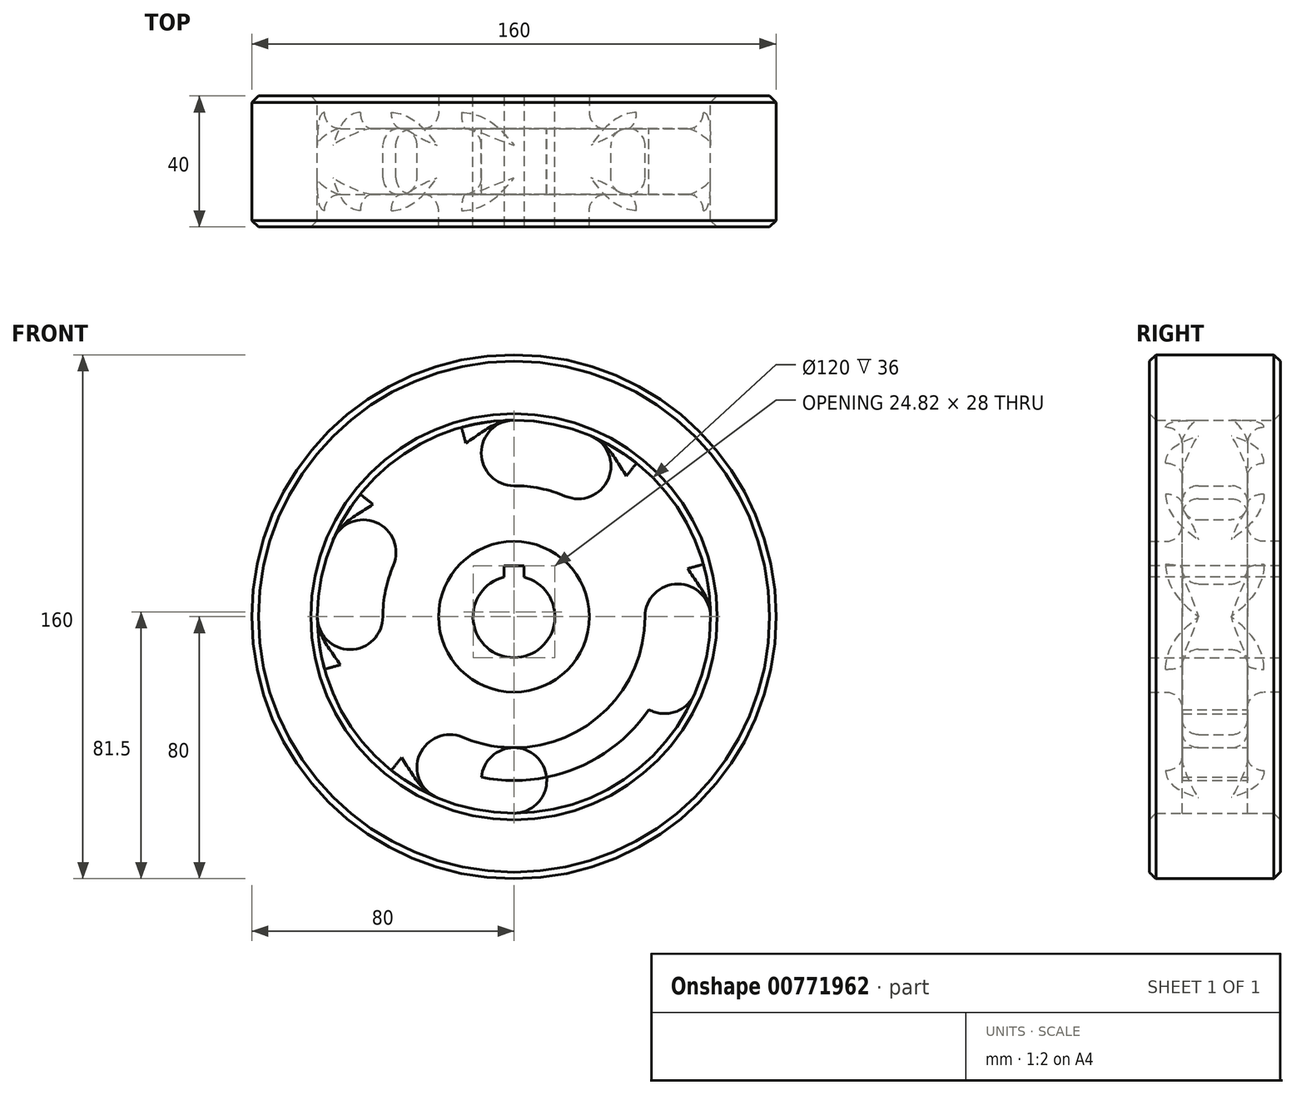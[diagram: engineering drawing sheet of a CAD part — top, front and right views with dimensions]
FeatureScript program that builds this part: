
annotation { "Feature Type Name" : "Feature", "Feature Type Description" : "" }
export const myFeature = defineFeature(function(context is Context, id is Id, definition is map)
    precondition{}
    {
        {
            var Q0;
            Q0=qCreatedBy(makeId("Front.planeOp"),FACE);
            var sketch = newSketch(context, id + "F0", { "sketchPlane" : qUnion([Q0])});
            skCircle(sketch, "E0", {"center": v(0, 0) * mm, "radius": 80 * mm});
            skCircle(sketch, "E1", {"center": v(0, 0) * mm, "radius": 60 * mm});
            skPoint(sketch, "E2", {"position": v(0, 60) * mm});
            skPoint(sketch, "E3", {"position": v(-60, 0) * mm});
            skPoint(sketch, "E4", {"position": v(60, 0) * mm});
            skPoint(sketch, "E5", {"position": v(0, -60) * mm});
            skCircle(sketch, "E6", {"center": v(0, 0) * mm, "radius": 50 * mm});
            skPoint(sketch, "E7", {"position": v(0, 50) * mm});
            skPoint(sketch, "E8", {"position": v(-50, 0) * mm});
            skPoint(sketch, "E9", {"position": v(0, -50) * mm});
            skPoint(sketch, "E10", {"position": v(50, 0) * mm});
            skCircle(sketch, "E11", {"center": v(0, 50) * mm, "radius": 10 * mm});
            skCircle(sketch, "E12", {"center": v(-50, 0) * mm, "radius": 10 * mm});
            skCircle(sketch, "E13", {"center": v(0, -50) * mm, "radius": 10 * mm});
            skCircle(sketch, "E14", {"center": v(50, 0) * mm, "radius": 10 * mm});
            skPoint(sketch, "E15", {"position": v(-46, 19.6) * mm});
            skPoint(sketch, "E16", {"position": v(19.6, 46) * mm});
            skPoint(sketch, "E17", {"position": v(46, -19.6) * mm});
            skPoint(sketch, "E18", {"position": v(-19.6, -46) * mm});
            skCircle(sketch, "E19", {"center": v(-46, 19.6) * mm, "radius": 10 * mm});
            skCircle(sketch, "E20", {"center": v(19.6, 46) * mm, "radius": 10 * mm});
            skCircle(sketch, "E21", {"center": v(46, -19.6) * mm, "radius": 10 * mm});
            skCircle(sketch, "E22", {"center": v(-19.6, -46) * mm, "radius": 10 * mm});
            skCircle(sketch, "E23", {"center": v(0, 0) * mm, "radius": 40 * mm});
            skCircle(sketch, "E24", {"center": v(0, 0) * mm, "radius": 23 * mm});
            skCircle(sketch, "E25", {"center": v(0, 0) * mm, "radius": 12.5 * mm});
            skSolve(sketch);
        }
        {
            var Q0;
            Q0=makeQuery(id+"F0.imprint","IMPRINT",FACE,{"disambiguationData":[TD([[makeQuery(id+"F0.imprint","IMPRINT",EDGE,{"derivedFrom":sQuery(id+"F0.wireOp",EDGE,"E0")}),1.0]])]});
            extrude(context, id + "F1", {"entities" : qUnion([Q0]), "depth" : 20 * mm, "offsetDistance" : 25 * mm});
        }
        {
            var Q0;
            {var subQ0=sQuery(id+"F0.wireOp",EDGE,"E11");var subQ1=sQuery(id+"F0.wireOp",EDGE,"E6");var subQ2=makeQuery(id+"F0.imprint","INTERSECT",VERTEX,{"disambiguationData":[OD(1.0)],"derivedFrom":[subQ1,subQ0]});Q0=makeQuery(id+"F0.imprint","IMPRINT",FACE,{"disambiguationData":[TD([[makeQuery(id+"F0.imprint","IMPRINT",EDGE,{"disambiguationData":[TD([[subQ2,-1.0]])],"derivedFrom":subQ1}),1.0]])]});}
            var Q1;
            {var subQ0=sQuery(id+"F0.wireOp",EDGE,"E11");var subQ1=sQuery(id+"F0.wireOp",EDGE,"E1");var subQ2=makeQuery(id+"F0.imprint","INTERSECT",VERTEX,{"derivedFrom":[subQ1,subQ0]});Q1=makeQuery(id+"F0.imprint","IMPRINT",FACE,{"disambiguationData":[TD([[makeQuery(id+"F0.imprint","IMPRINT",EDGE,{"disambiguationData":[TD([[subQ2,-1.0]])],"derivedFrom":subQ1}),1.0]])]});}
            var Q2;
            {var subQ0=sQuery(id+"F0.wireOp",EDGE,"E12");var subQ1=sQuery(id+"F0.wireOp",EDGE,"E1");var subQ2=makeQuery(id+"F0.imprint","INTERSECT",VERTEX,{"derivedFrom":[subQ1,subQ0]});Q2=makeQuery(id+"F0.imprint","IMPRINT",FACE,{"disambiguationData":[TD([[makeQuery(id+"F0.imprint","IMPRINT",EDGE,{"disambiguationData":[TD([[subQ2,-1.0]])],"derivedFrom":subQ1}),1.0]])]});}
            var Q3;
            {var subQ0=sQuery(id+"F0.wireOp",EDGE,"E12");var subQ1=sQuery(id+"F0.wireOp",EDGE,"E6");var subQ2=makeQuery(id+"F0.imprint","INTERSECT",VERTEX,{"disambiguationData":[OD(1.0)],"derivedFrom":[subQ1,subQ0]});Q3=makeQuery(id+"F0.imprint","IMPRINT",FACE,{"disambiguationData":[TD([[makeQuery(id+"F0.imprint","IMPRINT",EDGE,{"disambiguationData":[TD([[subQ2,-1.0]])],"derivedFrom":subQ1}),1.0]])]});}
            var Q4;
            {var subQ0=sQuery(id+"F0.wireOp",EDGE,"E13");var subQ1=sQuery(id+"F0.wireOp",EDGE,"E6");var subQ2=makeQuery(id+"F0.imprint","INTERSECT",VERTEX,{"disambiguationData":[OD(1.0)],"derivedFrom":[subQ1,subQ0]});Q4=makeQuery(id+"F0.imprint","IMPRINT",FACE,{"disambiguationData":[TD([[makeQuery(id+"F0.imprint","IMPRINT",EDGE,{"disambiguationData":[TD([[subQ2,-1.0]])],"derivedFrom":subQ1}),1.0]])]});}
            var Q5;
            {var subQ0=sQuery(id+"F0.wireOp",EDGE,"E13");var subQ1=sQuery(id+"F0.wireOp",EDGE,"E1");var subQ2=makeQuery(id+"F0.imprint","INTERSECT",VERTEX,{"derivedFrom":[subQ1,subQ0]});Q5=makeQuery(id+"F0.imprint","IMPRINT",FACE,{"disambiguationData":[TD([[makeQuery(id+"F0.imprint","IMPRINT",EDGE,{"disambiguationData":[TD([[subQ2,-1.0]])],"derivedFrom":subQ1}),1.0]])]});}
            var Q6;
            {var subQ0=sQuery(id+"F0.wireOp",EDGE,"E20");var subQ1=sQuery(id+"F0.wireOp",EDGE,"E6");var subQ2=makeQuery(id+"F0.imprint","INTERSECT",VERTEX,{"disambiguationData":[OD(0.0)],"derivedFrom":[subQ1,subQ0]});Q6=makeQuery(id+"F0.imprint","IMPRINT",FACE,{"disambiguationData":[TD([[makeQuery(id+"F0.imprint","IMPRINT",EDGE,{"disambiguationData":[TD([[subQ2,1.0]])],"derivedFrom":subQ1}),1.0]])]});}
            var Q7;
            {var subQ0=sQuery(id+"F0.wireOp",EDGE,"E20");var subQ1=sQuery(id+"F0.wireOp",EDGE,"E1");var subQ2=makeQuery(id+"F0.imprint","INTERSECT",VERTEX,{"derivedFrom":[subQ1,subQ0]});Q7=makeQuery(id+"F0.imprint","IMPRINT",FACE,{"disambiguationData":[TD([[makeQuery(id+"F0.imprint","IMPRINT",EDGE,{"disambiguationData":[TD([[subQ2,1.0]])],"derivedFrom":subQ1}),1.0]])]});}
            var Q8;
            Q8=makeQuery(id+"F0.imprint","IMPRINT",FACE,{"disambiguationData":[TD([[makeQuery(id+"F0.imprint","IMPRINT",EDGE,{"derivedFrom":sQuery(id+"F0.wireOp",EDGE,"E24")}),-1.0]])]});
            extrude(context, id + "F2", {"entities" : qUnion([Q0, Q1, Q2, Q3, Q4, Q5, Q6, Q7, Q8]), "operationType" : NewBodyOperationType.ADD, "depth" : 10 * mm, "offsetDistance" : 25 * mm});
        }
        {
            var Q0;
            Q0=makeQuery(id+"F0.imprint","IMPRINT",FACE,{"disambiguationData":[TD([[makeQuery(id+"F0.imprint","IMPRINT",EDGE,{"derivedFrom":sQuery(id+"F0.wireOp",EDGE,"E24")}),1.0]])]});
            extrude(context, id + "F3", {"entities" : qUnion([Q0]), "operationType" : NewBodyOperationType.ADD, "depth" : 20 * mm, "offsetDistance" : 25 * mm});
        }
        {
            var Q0;
            Q0=makeQuery(id+"F0.imprint","IMPRINT",FACE,{"disambiguationData":[TD([[makeQuery(id+"F0.imprint","IMPRINT",EDGE,{"derivedFrom":sQuery(id+"F0.wireOp",EDGE,"E0")}),1.0]])]});
            var Q1;
            Q1=makeQuery(id+"F0.imprint","IMPRINT",FACE,{"disambiguationData":[TD([[makeQuery(id+"F0.imprint","IMPRINT",EDGE,{"derivedFrom":sQuery(id+"F0.wireOp",EDGE,"E24")}),1.0]])]});
            extrude(context, id + "F4", {"entities" : qUnion([Q0, Q1]), "operationType" : NewBodyOperationType.ADD, "depth" : 20 * mm, "offsetDistance" : 25 * mm});
        }
        {
            var Q0;
            Q0=makeQuery(id+"F0.imprint","IMPRINT",FACE,{"disambiguationData":[TD([[makeQuery(id+"F0.imprint","IMPRINT",EDGE,{"derivedFrom":sQuery(id+"F0.wireOp",EDGE,"E0")}),1.0]])]});
            var Q1;
            Q1=makeQuery(id+"F0.imprint","IMPRINT",FACE,{"disambiguationData":[TD([[makeQuery(id+"F0.imprint","IMPRINT",EDGE,{"derivedFrom":sQuery(id+"F0.wireOp",EDGE,"E24")}),1.0]])]});
            extrude(context, id + "F5", {"entities" : qUnion([Q0, Q1]), "operationType" : NewBodyOperationType.ADD, "oppositeDirection" : true, "depth" : 20 * mm, "offsetDistance" : 25 * mm});
        }
        {
            var Q0;
            {var subQ0=sQuery(id+"F0.wireOp",EDGE,"E20");var subQ1=sQuery(id+"F0.wireOp",EDGE,"E6");var subQ2=makeQuery(id+"F0.imprint","INTERSECT",VERTEX,{"disambiguationData":[OD(0.0)],"derivedFrom":[subQ1,subQ0]});Q0=makeQuery(id+"F0.imprint","IMPRINT",FACE,{"disambiguationData":[TD([[makeQuery(id+"F0.imprint","IMPRINT",EDGE,{"disambiguationData":[TD([[subQ2,1.0]])],"derivedFrom":subQ1}),1.0]])]});}
            var Q1;
            {var subQ0=sQuery(id+"F0.wireOp",EDGE,"E20");var subQ1=sQuery(id+"F0.wireOp",EDGE,"E1");var subQ2=makeQuery(id+"F0.imprint","INTERSECT",VERTEX,{"derivedFrom":[subQ1,subQ0]});Q1=makeQuery(id+"F0.imprint","IMPRINT",FACE,{"disambiguationData":[TD([[makeQuery(id+"F0.imprint","IMPRINT",EDGE,{"disambiguationData":[TD([[subQ2,1.0]])],"derivedFrom":subQ1}),1.0]])]});}
            var Q2;
            {var subQ0=sQuery(id+"F0.wireOp",EDGE,"E13");var subQ1=sQuery(id+"F0.wireOp",EDGE,"E6");var subQ2=makeQuery(id+"F0.imprint","INTERSECT",VERTEX,{"disambiguationData":[OD(1.0)],"derivedFrom":[subQ1,subQ0]});Q2=makeQuery(id+"F0.imprint","IMPRINT",FACE,{"disambiguationData":[TD([[makeQuery(id+"F0.imprint","IMPRINT",EDGE,{"disambiguationData":[TD([[subQ2,-1.0]])],"derivedFrom":subQ1}),1.0]])]});}
            var Q3;
            {var subQ0=sQuery(id+"F0.wireOp",EDGE,"E13");var subQ1=sQuery(id+"F0.wireOp",EDGE,"E1");var subQ2=makeQuery(id+"F0.imprint","INTERSECT",VERTEX,{"derivedFrom":[subQ1,subQ0]});Q3=makeQuery(id+"F0.imprint","IMPRINT",FACE,{"disambiguationData":[TD([[makeQuery(id+"F0.imprint","IMPRINT",EDGE,{"disambiguationData":[TD([[subQ2,-1.0]])],"derivedFrom":subQ1}),1.0]])]});}
            var Q4;
            {var subQ0=sQuery(id+"F0.wireOp",EDGE,"E12");var subQ1=sQuery(id+"F0.wireOp",EDGE,"E1");var subQ2=makeQuery(id+"F0.imprint","INTERSECT",VERTEX,{"derivedFrom":[subQ1,subQ0]});Q4=makeQuery(id+"F0.imprint","IMPRINT",FACE,{"disambiguationData":[TD([[makeQuery(id+"F0.imprint","IMPRINT",EDGE,{"disambiguationData":[TD([[subQ2,-1.0]])],"derivedFrom":subQ1}),1.0]])]});}
            var Q5;
            {var subQ0=sQuery(id+"F0.wireOp",EDGE,"E12");var subQ1=sQuery(id+"F0.wireOp",EDGE,"E6");var subQ2=makeQuery(id+"F0.imprint","INTERSECT",VERTEX,{"disambiguationData":[OD(1.0)],"derivedFrom":[subQ1,subQ0]});Q5=makeQuery(id+"F0.imprint","IMPRINT",FACE,{"disambiguationData":[TD([[makeQuery(id+"F0.imprint","IMPRINT",EDGE,{"disambiguationData":[TD([[subQ2,-1.0]])],"derivedFrom":subQ1}),1.0]])]});}
            var Q6;
            {var subQ0=sQuery(id+"F0.wireOp",EDGE,"E11");var subQ1=sQuery(id+"F0.wireOp",EDGE,"E6");var subQ2=makeQuery(id+"F0.imprint","INTERSECT",VERTEX,{"disambiguationData":[OD(1.0)],"derivedFrom":[subQ1,subQ0]});Q6=makeQuery(id+"F0.imprint","IMPRINT",FACE,{"disambiguationData":[TD([[makeQuery(id+"F0.imprint","IMPRINT",EDGE,{"disambiguationData":[TD([[subQ2,-1.0]])],"derivedFrom":subQ1}),1.0]])]});}
            var Q7;
            {var subQ0=sQuery(id+"F0.wireOp",EDGE,"E11");var subQ1=sQuery(id+"F0.wireOp",EDGE,"E1");var subQ2=makeQuery(id+"F0.imprint","INTERSECT",VERTEX,{"derivedFrom":[subQ1,subQ0]});Q7=makeQuery(id+"F0.imprint","IMPRINT",FACE,{"disambiguationData":[TD([[makeQuery(id+"F0.imprint","IMPRINT",EDGE,{"disambiguationData":[TD([[subQ2,-1.0]])],"derivedFrom":subQ1}),1.0]])]});}
            var Q8;
            Q8=makeQuery(id+"F0.imprint","IMPRINT",FACE,{"disambiguationData":[TD([[makeQuery(id+"F0.imprint","IMPRINT",EDGE,{"derivedFrom":sQuery(id+"F0.wireOp",EDGE,"E24")}),-1.0]])]});
            extrude(context, id + "F6", {"entities" : qUnion([Q0, Q1, Q2, Q3, Q4, Q5, Q6, Q7, Q8]), "operationType" : NewBodyOperationType.ADD, "oppositeDirection" : true, "depth" : 10 * mm, "offsetDistance" : 25 * mm});
        }
        {
            var Q0;
            {var subQ0=sQuery(id+"F0.wireOp",EDGE,"E1");Q0=makeQuery(id+"F6.opExtrude","CAP_EDGE",EDGE,{"disambiguationData":[OSD([subQ0]),TDD([makeQuery(id+"F0.imprint","IMPRINT",EDGE,{"disambiguationData":[TD([[makeQuery(id+"F0.imprint","INTERSECT",VERTEX,{"derivedFrom":[subQ0,sQuery(id+"F0.wireOp",EDGE,"E20")]}),1.0]])],"derivedFrom":subQ0})])],"isStart":false});}
            var Q1;
            {var subQ0=sQuery(id+"F0.wireOp",EDGE,"E1");Q1=makeQuery(id+"F6.opExtrude","CAP_EDGE",EDGE,{"disambiguationData":[OSD([subQ0]),TDD([makeQuery(id+"F0.imprint","IMPRINT",EDGE,{"disambiguationData":[TD([[makeQuery(id+"F0.imprint","INTERSECT",VERTEX,{"derivedFrom":[subQ0,sQuery(id+"F0.wireOp",EDGE,"E13")]}),-1.0]])],"derivedFrom":subQ0})])],"isStart":false});}
            var Q2;
            Q2=makeQuery(id+"F6.opExtrude","CAP_FACE",FACE,{"disambiguationData":[OSD([sQuery(id+"F0.wireOp",EDGE,"E1"),sQuery(id+"F0.wireOp",EDGE,"E11"),sQuery(id+"F0.wireOp",EDGE,"E12"),sQuery(id+"F0.wireOp",EDGE,"E13"),sQuery(id+"F0.wireOp",EDGE,"E14"),sQuery(id+"F0.wireOp",EDGE,"E19"),sQuery(id+"F0.wireOp",EDGE,"E20"),sQuery(id+"F0.wireOp",EDGE,"E21"),sQuery(id+"F0.wireOp",EDGE,"E22"),sQuery(id+"F0.wireOp",EDGE,"E23"),sQuery(id+"F0.wireOp",EDGE,"E24")])],"isStart":false});
            var Q3;
            Q3=makeQuery(id+"F2.opExtrude","CAP_FACE",FACE,{"disambiguationData":[OSD([sQuery(id+"F0.wireOp",EDGE,"E1"),sQuery(id+"F0.wireOp",EDGE,"E11"),sQuery(id+"F0.wireOp",EDGE,"E12"),sQuery(id+"F0.wireOp",EDGE,"E13"),sQuery(id+"F0.wireOp",EDGE,"E14"),sQuery(id+"F0.wireOp",EDGE,"E19"),sQuery(id+"F0.wireOp",EDGE,"E20"),sQuery(id+"F0.wireOp",EDGE,"E21"),sQuery(id+"F0.wireOp",EDGE,"E22"),sQuery(id+"F0.wireOp",EDGE,"E23"),sQuery(id+"F0.wireOp",EDGE,"E24")])],"isStart":false});
            fillet(context, id + "F7", {"entities" : qUnion([Q0, Q1, Q2, Q3]), "radius" : 5 * mm, "tangentPropagation" : true, "allowEdgeOverflow" : false});
        }
        {
            var Q0;
            Q0=makeQuery(id+"F5.opExtrude","CAP_EDGE",EDGE,{"disambiguationData":[OSD([sQuery(id+"F0.wireOp",EDGE,"E0")])],"isStart":false});
            var Q1;
            Q1=makeQuery(id+"F5.opExtrude","CAP_EDGE",EDGE,{"disambiguationData":[OSD([sQuery(id+"F0.wireOp",EDGE,"E1")])],"isStart":false});
            var Q2;
            Q2=makeQuery(id+"F1.opExtrude","CAP_FACE",FACE,{"disambiguationData":[OSD([sQuery(id+"F0.wireOp",EDGE,"E0"),sQuery(id+"F0.wireOp",EDGE,"E1")])],"isStart":false});
            chamfer(context, id + "F8", {"entities" : qUnion([Q0, Q1, Q2]), "width" : 2 * mm, "tangentPropagation" : true});
        }
        {
            var Q0;
            Q0=makeQuery(id+"F3.opExtrude","CAP_FACE",FACE,{"disambiguationData":[OSD([sQuery(id+"F0.wireOp",EDGE,"E24"),sQuery(id+"F0.wireOp",EDGE,"E25")])],"isStart":false});
            var sketch = newSketch(context, id + "F9", { "sketchPlane" : qUnion([Q0])});
            skPoint(sketch, "E26", {"position": v(0, 3.36) * mm});
            skPoint(sketch, "E27", {"position": v(0, 15.5) * mm});
            skPoint(sketch, "E28", {"position": v(0, 12.5) * mm});
            skLineSegment(sketch, "E29", {"start": v(0, 15.5) * mm, "end": v(-6, 15.5) * mm});
            skLineSegment(sketch, "E30", {"start": v(-6, 15.5) * mm, "end": v(5.27, 15.5) * mm});
            skPoint(sketch, "E31", {"position": v(3, 15.5) * mm});
            skPoint(sketch, "E32", {"position": v(-3, 15.5) * mm});
            skLineSegment(sketch, "E33", {"start": v(-3, 15.5) * mm, "end": v(-3, 12.13) * mm});
            skLineSegment(sketch, "E34", {"start": v(-3, 12.13) * mm, "end": v(3, 12.13) * mm});
            skLineSegment(sketch, "E35", {"start": v(3, 12.13) * mm, "end": v(3, 15.5) * mm});
            skSolve(sketch);
        }
        {
            var Q0;
            {var subQ1=sQuery(id+"F9.wireOp",EDGE,"E33");Q0=makeQuery(id+"F9.imprint","IMPRINT",FACE,{"disambiguationData":[TD([[makeQuery(id+"F9.imprint","IMPRINT",EDGE,{"derivedFrom":subQ1}),1.0]])]});}
            extrude(context, id + "F10", {"entities" : qUnion([Q0]), "operationType" : NewBodyOperationType.REMOVE, "oppositeDirection" : true, "depth" : 50 * mm, "offsetDistance" : 25 * mm});
        }
    });
